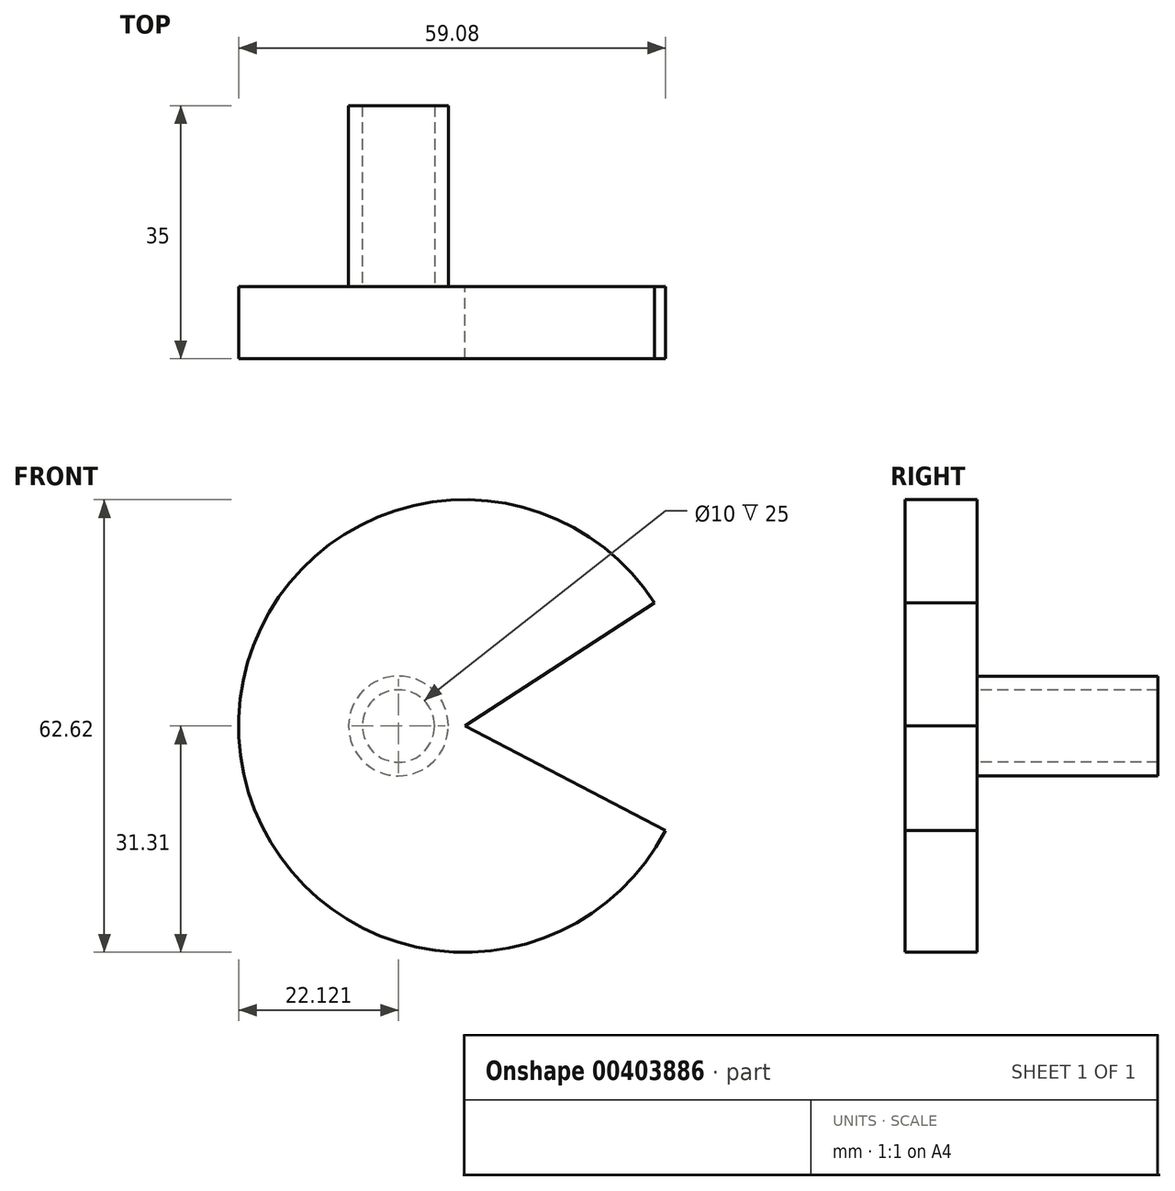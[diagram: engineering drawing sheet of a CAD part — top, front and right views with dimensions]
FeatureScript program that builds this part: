
annotation { "Feature Type Name" : "Feature", "Feature Type Description" : "" }
export const myFeature = defineFeature(function(context is Context, id is Id, definition is map)
    precondition{}
    {
        {
            var Q0;
            Q0=qCreatedBy(makeId("Front.planeOp"),FACE);
            var sketch = newSketch(context, id + "F0", { "sketchPlane" : qUnion([Q0])});
            skArc(sketch, "E0", {"start": v(26.27, 17.04) * mm, "mid": v(-31.28, -1.49) * mm, "end": v(27.77, -14.47) * mm});
            skLineSegment(sketch, "E1", {"start": v(0, 0) * mm, "end": v(26.27, 17.04) * mm});
            skLineSegment(sketch, "E2", {"start": v(0, 0) * mm, "end": v(27.77, -14.47) * mm});
            skSolve(sketch);
        }
        {
            var Q0;
            Q0=makeQuery(id+"F0.imprint","IMPRINT",FACE,{"disambiguationData":[TD([[makeQuery(id+"F0.imprint","IMPRINT",EDGE,{"derivedFrom":sQuery(id+"F0.wireOp",EDGE,"E0")}),1.0]])]});
            extrude(context, id + "F1", {"entities" : qUnion([Q0]), "depth" : 10 * mm});
        }
        {
            var Q0;
            Q0=makeQuery(id+"F1.opExtrude","CAP_FACE",FACE,{"disambiguationData":[OSD([sQuery(id+"F0.wireOp",EDGE,"E0"),sQuery(id+"F0.wireOp",EDGE,"E1"),sQuery(id+"F0.wireOp",EDGE,"E2")])],"isStart":true});
            var sketch = newSketch(context, id + "F2", { "sketchPlane" : qUnion([Q0])});
            skCircle(sketch, "E3", {"center": v(9.19, 0) * mm, "radius": 6.9 * mm});
            skCircle(sketch, "E4", {"center": v(9.19, 0) * mm, "radius": 5 * mm});
            skSolve(sketch);
        }
        {
            var Q0;
            Q0=makeQuery(id+"F2.imprint","IMPRINT",FACE,{"disambiguationData":[TD([[makeQuery(id+"F2.imprint","IMPRINT",EDGE,{"derivedFrom":sQuery(id+"F2.wireOp",EDGE,"E3")}),1.0]])]});
            extrude(context, id + "F3", {"entities" : qUnion([Q0]), "operationType" : NewBodyOperationType.ADD, "depth" : 25 * mm, "offsetDistance" : 25 * mm});
        }
    });
